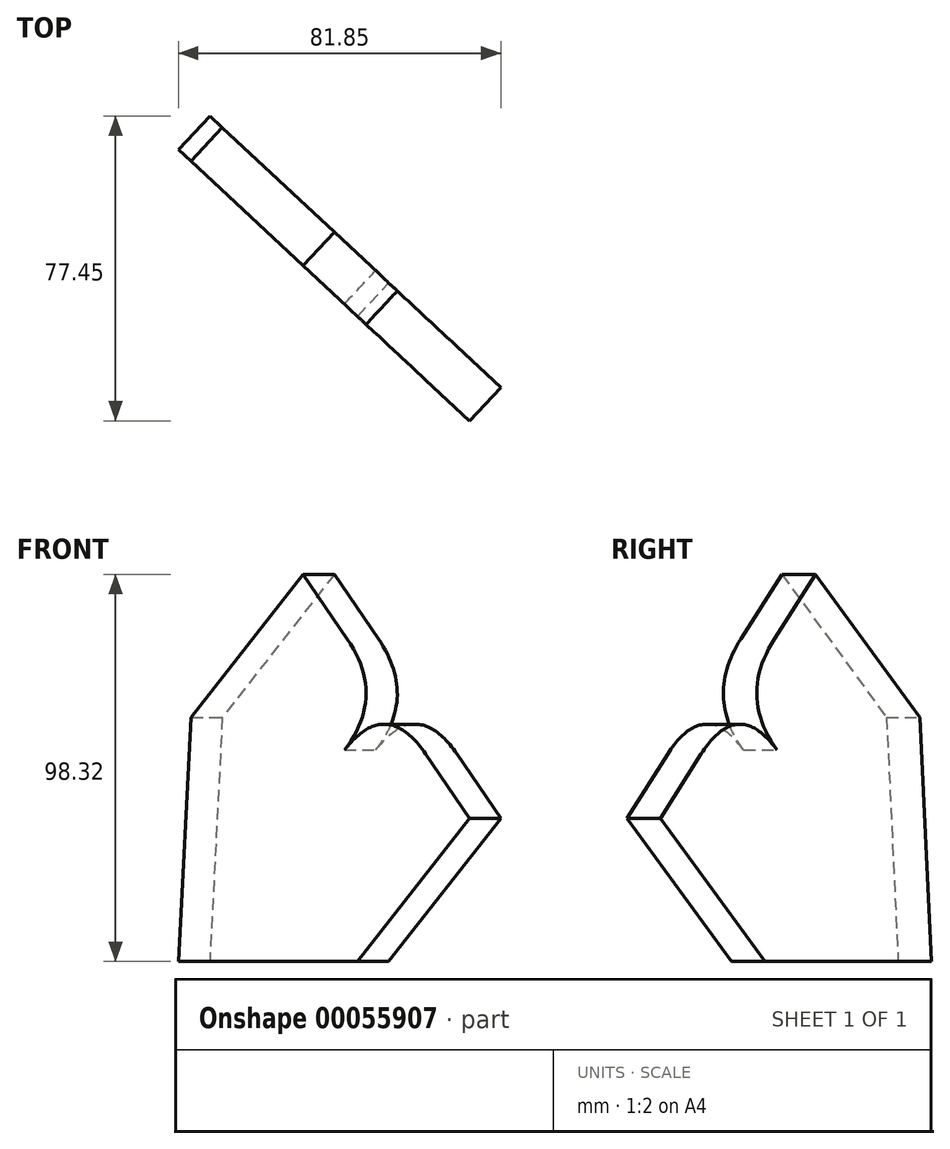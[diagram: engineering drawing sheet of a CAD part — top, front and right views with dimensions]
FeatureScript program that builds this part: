
annotation { "Feature Type Name" : "Feature", "Feature Type Description" : "" }
export const myFeature = defineFeature(function(context is Context, id is Id, definition is map)
    precondition{}
    {
        {
            var Q0;
            Q0=qCreatedBy(makeId("Top.planeOp"),FACE);
            var sketch = newSketch(context, id + "F0", { "sketchPlane" : qUnion([Q0])});
            skLineSegment(sketch, "E0", {"start": v(0, 0) * mm, "end": v(98.7, 0) * mm});
            skLineSegment(sketch, "E1", {"start": v(98.7, 0) * mm, "end": v(98.7, 42.38) * mm});
            skLineSegment(sketch, "E2", {"start": v(98.7, 42.38) * mm, "end": v(45.44, 42.38) * mm});
            skLineSegment(sketch, "E3", {"start": v(45.44, 42.38) * mm, "end": v(0, 0) * mm});
            skSolve(sketch);
        }
        {
            var Q0;
            Q0 = qSketchRegion(id + "F0", true);
            extrude(context, id + "F1", {"entities" : qUnion([Q0]), "depth" : 11.63 * mm});
        }
        {
            var Q0;
            Q0=makeQuery(id+"F1.opExtrude","SWEPT_EDGE",EDGE,{"disambiguationData":[OSD([sQuery(id+"F0.wireOp",EDGE,"E0"),sQuery(id+"F0.wireOp",EDGE,"E1")])]});
            fillet(context, id + "F2", {"entities" : qUnion([Q0]), "radius" : 20 * mm, "tangentPropagation" : true, "rho" : 0.5, "crossSection" : FilletCrossSection.CONIC, "allowEdgeOverflow" : false});
        }
        {
            var Q0;
            Q0=makeQuery(id+"F1.opExtrude","SWEPT_BODY",BODY,{"disambiguationData":[OSD([sQuery(id+"F0.wireOp",EDGE,"E0"),sQuery(id+"F0.wireOp",EDGE,"E1"),sQuery(id+"F0.wireOp",EDGE,"E2"),sQuery(id+"F0.wireOp",EDGE,"E3")])]});
            var Q1;
            Q1=qCreatedBy(makeId("Front.planeOp"),FACE);
            mirror(context, id + "F3", {"operationType" : NewBodyOperationType.ADD, "entities" : qUnion([Q0]), "mirrorPlane" : qUnion([Q1])});
        }
        {
            var Q0;
            Q0=makeQuery(id+"F1.opExtrude","SWEPT_BODY",BODY,{"disambiguationData":[OSD([sQuery(id+"F0.wireOp",EDGE,"E0"),sQuery(id+"F0.wireOp",EDGE,"E1"),sQuery(id+"F0.wireOp",EDGE,"E2"),sQuery(id+"F0.wireOp",EDGE,"E3")])]});
            var Q1;
            Q1=makeQuery(id+"F3.opPattern","COPY",EDGE,{"derivedFrom":makeQuery(id+"F1.opExtrude","CAP_EDGE",EDGE,{"disambiguationData":[OSD([sQuery(id+"F0.wireOp",EDGE,"E3")])],"isStart":false}),"instanceName":"1"});
            transform(context, id + "F4", {"entities" : qUnion([Q0]), "transformType" : TransformType.ROTATION, "transformAxis" : qUnion([Q1]), "angle" : 90 * degree, "oppositeDirection" : true, "makeCopy" : false});
        }
    });
